# Revit family: Shower-Whitehall-BestCare-WH418ADA-CSHS-R_Series
name_source: partatom
category: Plumbing Fixtures
units: mm (PartAtom-declared; Revit-internal decimal feet)

## family parameters
Cut with Voids When Loaded = Yes
Host = Face
Maintain Annotation Orientation = No
OmniClass Number = 23.45.05.14.17
OmniClass Title = Showers
Part Type = Normal
Room Calculation Point = No
Round Connector Dimension = Use Diameter
Shared = Yes

## types (2) — shared parameters
ADA Compliant = Yes
Assembly Code = D2010710
CW Connection = Yes
CWFU = 3
Conical Shower Head with Swivel Adjustment- CSHS series at 48" Discharge max. = Yes
Conical Shower Head with Swivel Adjustment- CSHS series at 72" Discharge. = Yes
Control Area- CBC Standard Roll-In Stall Type Shown. See Dimensional Details. = Yes
Control Valve- WHSV16 Mixing Valve with Tri-Lever Handle (Standard). = Yes
Default Elevation = 72"
Description = BestCare® Ligature-Resistant ADA and CBC (Calif Title 24) Compliant Wall Shower with Dual Fixed Adjustable Showerhead
Diverter Valve- WHDIV with Tri-Lever Handle (Standard). = Yes
Flow Rate = 1.5 GPM
HW Connection = Yes
HWFU = 3
IAPMO Compliance = Mixing Valve meets criteria for temperature and pressure changes,
defined by ASSE 1016. Valve conforms with lead free requirements of NSF61, Section 9, 1997 and CHSC 116875.
Installation Type = Recessed Wall Mounted
L Left Side = No
Manufacturer = Whitehall Mfg.
Material = Metal-Whitehall-304-Stainless_Steel-16_Gauge
Mounting Frame Material = Metal-Whitehall-304-Stainless_Steel-16_Gauge
Panel Material = Metal-Whitehall-304-Stainless-Steel-18_Gauge
Price = Prices may vary. Please consult Manufacturer Representative for most up-to-date price list.
Product Documentation Link = https://www.whitehallmfg.com
Product Page URL = https://www.whitehallmfg.com
R Right Side = Yes
Showerhead Material = Metal-Whitehall-Chrome_Plated-Brass
Tempered Water Connection Diameter = 1/2"
Tri-Lever Handle Diameter = 5 1/2"
Tri-Lever Handle Material = Metal-Whitehall-Chrome_Plated-Brass
URL = https://www.whitehallmfg.com
Vent Connection = No
Wall Mounting Frame with Plaster Flanges = Yes
Waste Connection = No
cUPC Compliant = Yes
zero-valued in all types: WFU

## per-type parameters (varying)
| type | Cold Water Connection Diameter | Cold Water Connection Radius | Hot Water Connection Diameter | Hot Water Connection Radius | Recessed Soap Dish- WH1832 series (Specify). | Soap Dish Extrusion |
| WH418ADA-CSHS-R | 1/2" | 1/4" | 1/2" | 1/4" | Yes | 0" |
| WH418ADA-CSHS-LRD-R | 1" | 1/2" | 1" | 1/2" | No | 7/32" |

note: column(s) folded — value = type name in every type: Model

## geometry (parser evidence)
native form markers: Sweep x4
no freeform markers — native parametric forms only
